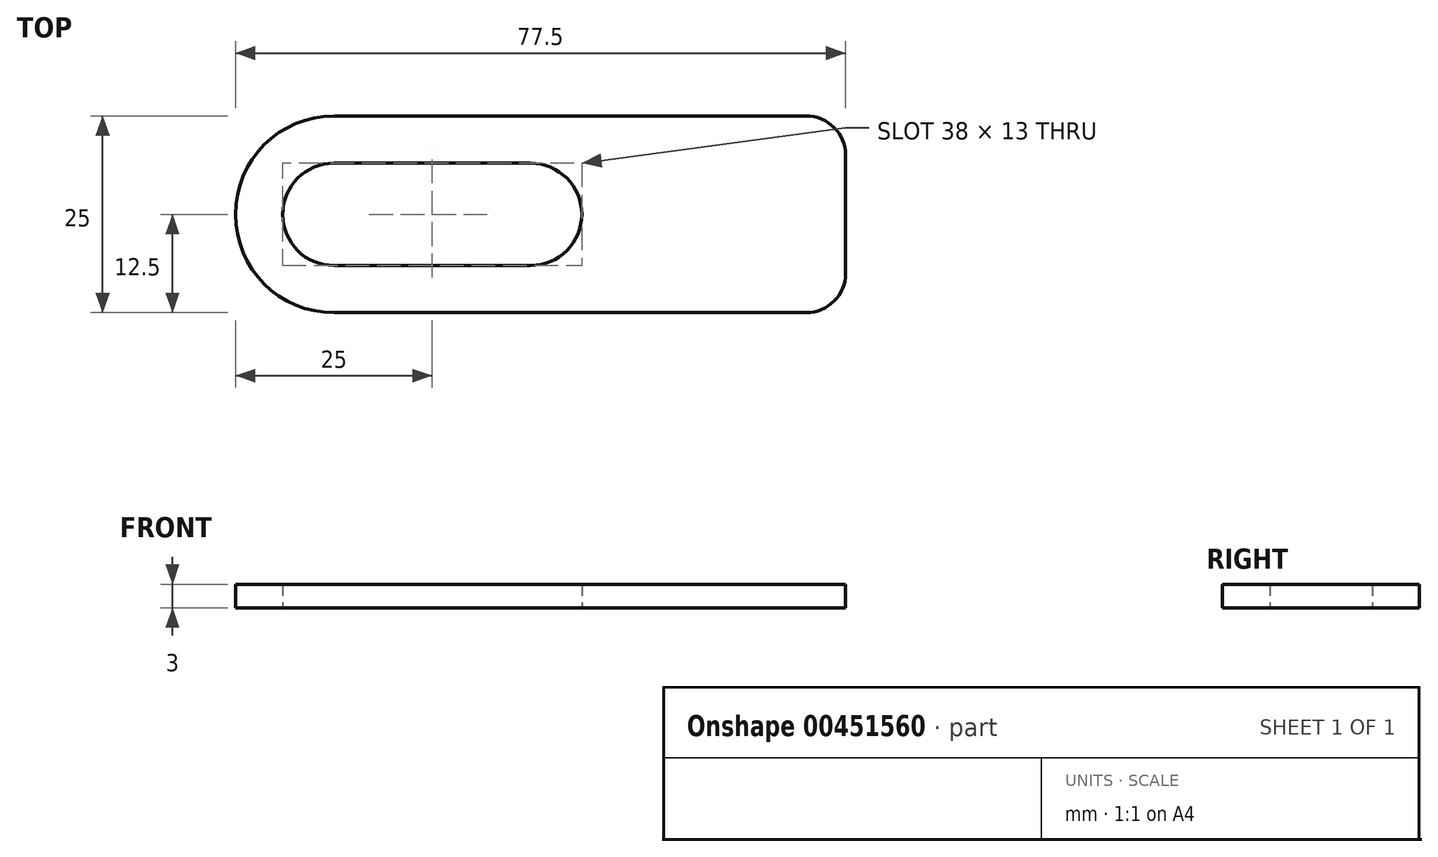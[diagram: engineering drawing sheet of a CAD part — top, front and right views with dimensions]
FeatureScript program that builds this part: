
annotation { "Feature Type Name" : "Feature", "Feature Type Description" : "" }
export const myFeature = defineFeature(function(context is Context, id is Id, definition is map)
    precondition{}
    {
        {
            var Q0;
            Q0=qCreatedBy(makeId("Top.planeOp"),FACE);
            var sketch = newSketch(context, id + "F0", { "sketchPlane" : qUnion([Q0])});
            skLineSegment(sketch, "E0.bottom", {"start": v(0, 0) * mm, "end": v(60, 0) * mm});
            skLineSegment(sketch, "E0.top", {"start": v(0, 25) * mm, "end": v(60, 25) * mm});
            skLineSegment(sketch, "E0.left", {"start": v(0, 0) * mm, "end": v(0, 25) * mm});
            skLineSegment(sketch, "E0.right", {"start": v(65, 5) * mm, "end": v(65, 20) * mm});
            skArc(sketch, "E1", {"start": v(0, 25) * mm, "mid": v(-12.5, 12.5) * mm, "end": v(0, 0) * mm});
            skLineSegment(sketch, "E2", {"start": v(0, 19) * mm, "end": v(25, 19) * mm});
            skLineSegment(sketch, "E3", {"start": v(0, 6) * mm, "end": v(25, 6) * mm});
            skArc(sketch, "E4", {"start": v(25, 6) * mm, "mid": v(31.5, 12.5) * mm, "end": v(25, 19) * mm});
            skArc(sketch, "E5", {"start": v(0, 19) * mm, "mid": v(-6.5, 12.5) * mm, "end": v(0, 6) * mm});
            skPoint(sketch, "E6.visualSharp", {"position": v(65, 25) * mm});
            skArc(sketch, "E6.filletArc", {"start": v(65, 20) * mm, "mid": v(63.54, 23.54) * mm, "end": v(60, 25) * mm});
            skPoint(sketch, "E7.visualSharp", {"position": v(65, 0) * mm});
            skArc(sketch, "E7.filletArc", {"start": v(60, 0) * mm, "mid": v(63.54, 1.46) * mm, "end": v(65, 5) * mm});
            skSolve(sketch);
        }
        {
            var Q0;
            {var subQ5=sQuery(id+"F0.wireOp",EDGE,"E0.bottom");Q0=makeQuery(id+"F0.imprint","IMPRINT",FACE,{"disambiguationData":[TD([[makeQuery(id+"F0.imprint","IMPRINT",EDGE,{"derivedFrom":subQ5}),1.0]])]});}
            var Q1;
            {var subQ0=sQuery(id+"F0.wireOp",EDGE,"E1");Q1=makeQuery(id+"F0.imprint","IMPRINT",FACE,{"disambiguationData":[TD([[makeQuery(id+"F0.imprint","IMPRINT",EDGE,{"derivedFrom":subQ0}),1.0]])]});}
            extrude(context, id + "F1", {"entities" : qUnion([Q0, Q1]), "depth" : 3 * mm, "offsetDistance" : 25 * mm});
        }
    });
